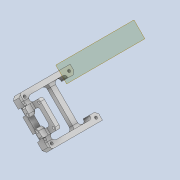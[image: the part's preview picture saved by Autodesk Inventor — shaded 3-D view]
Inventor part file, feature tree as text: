
AUTODESK INVENTOR PART (.ipt)
format: ipt  version: 2020 (Build 240168000, 168)  size: 592,384 bytes
history: native  units: mm
features: projected_geometry x16, sketch x12, extrude x10, thicken_offset x9, fillet x8, other x6, chamfer x5, hole x2, plane x1, reference x1
ambient origin geometry x8: Origin, YZ Plane, XZ Plane, XY Plane, X Axis, Y Axis, Z Axis, Center Point
bodies: Solid1 (feature_tree)
feature tree (70):
  extrude  "Extrusion1"  Depth=4.0mm
  extrude  "Extrusion2"  Depth=4.0mm
  extrude  "Extrusion3"  Depth=2.0mm
  thicken_offset  "Thicken1"
  thicken_offset  "Thicken2"
  thicken_offset  "Thicken3"
  thicken_offset  "Thicken4"
  chamfer  "Chamfer2"  Distance=6.3mm
  fillet  "Fillet5"  Radius=6.0mm
  hole  "Hole1"  [1 undecoded]
  hole  "Hole2"  [1 undecoded]
  plane  "Work Plane1"
  extrude  "Extrusion4"  Depth=0.25mm
  extrude  "Extrusion5"  Depth=0.25mm
  extrude  "Extrusion6"  Depth=1.0mm
  thicken_offset  "Thicken5"
  thicken_offset  "Thicken6"
  thicken_offset  "Thicken7"
  fillet  "Fillet8"  Radius=1.0mm
  chamfer  "Chamfer3"  Distance=1.0mm Angle=45.0deg
  fillet  "Fillet9"  Radius=2.0mm
  fillet  "Fillet10"  Radius=6.0mm
  fillet  "Fillet11"  Radius=6.0mm
  chamfer  "Chamfer4"  Distance=6.0mm
  extrude  "Extrusion7"  Depth=6.0mm
  fillet  "Fillet12"  Radius=35.0mm
  chamfer  "Chamfer5"  Distance=3.5mm
  extrude  "Extrusion8"  Depth=0.5mm
  fillet  "Fillet13"  Radius=3.5mm
  chamfer  "Chamfer6"  Distance=6.3mm
  fillet  "Fillet14"  Radius=6.3mm
  thicken_offset  "Thicken8"
  thicken_offset  "Thicken9"
  extrude  "Extrusion9"  Depth=0.5mm
  extrude  "Extrusion10"  Depth=0.5mm
  sketch  "Sketch1"  dims[d0=4.0mm d1=4.0mm]
  reference  "Reference1"
  sketch  "Sketch2"  dims[d2=4.0mm d3=4.0mm]
  projected_geometry  "Projected Loop1"
  sketch  "Sketch3"  dims[d4=2.0mm d5=0.0mm d6=5.5mm]
  projected_geometry  "Projected Loop2"
  projected_geometry  "Projected Loop3"
  projected_geometry  "Projected Loop4"
  sketch  "Sketch4"  dims[d7=4.0mm]
  projected_geometry  "Projected Loop5"
  projected_geometry  "Projected Loop6"
  sketch  "Sketch5"  dims[d8=4.0mm]
  projected_geometry  "Projected Loop7"
  projected_geometry  "Projected Loop8"
  sketch  "Sketch6"  dims[d9=4.0mm d10=6.3mm d11=0.0mm d12=6.0mm]
  sketch  "Sketch7"  dims[d13=4.0mm d14=6.0mm]
  projected_geometry  "Projected Loop9"
  projected_geometry  "Projected Loop10"
  sketch  "Sketch8"  dims[d15=4.0mm d16=6.0mm d17=0.0mm]
  projected_geometry  "Projected Loop11"
  sketch  "Sketch9"  dims[d21=0.25mm d22=0.25mm]
  projected_geometry  "Projected Loop12"
  sketch  "Sketch10"  dims[d23=0.25mm d24=0.25mm]
  projected_geometry  "Projected Loop13"
  sketch  "Sketch11"  dims[d27=1.0mm d28=1.0mm d29=1.0mm]
  projected_geometry  "Projected Loop14"
  projected_geometry  "Projected Loop15"
  sketch  "Sketch12"  dims[d30=1.0mm d33=1.0mm d34=2.0mm d35=45.0deg d36=2.0mm d37=1.9mm d38=6.0mm d39=4.0mm d40=2.0mm d41=90.0deg d42=4.0mm d43=0.0mm d44=1.9mm d45=6.0mm d46=4.0mm d47=2.0mm d48=90.0deg d49=4.0mm d50=0.0mm d51=6.0mm d52=6.0mm d53=6.0mm d54=6.0mm d55=35.0mm d56=3.5mm d57=35.0mm d58=3.5mm d59=6.3mm d60=0.0mm d61=6.3mm d62=0.0mm d63=1.9mm d64=1.9mm d65=6.3mm d66=0.0mm d69=1.5mm d70=1.5mm d71=1.0mm d72=1.5mm d73=1.0mm d74=1.5mm d75=3.0mm d76=1.0mm d77=2.0mm d78=45.0deg d79=1.0mm d80=0.5mm d81=0.5mm d82=2.0mm d83=2.0mm d84=45.0deg d85=5.0mm d86=5.0mm d87=5.0mm d88=5.0mm d89=2.0mm d90=0.0mm d91=3.0mm d92=1.0mm d93=2.0mm d94=45.0deg d95=7.0mm d96=29.0mm d97=4.0mm d98=3.5mm d99=0.0mm d100=2.2mm d101=2.0mm d102=2.0mm d103=45.0deg d104=2.0mm d105=0.06mm d106=0.06mm d107=0.06mm d108=0.06mm d109=2.0mm d110=2.0mm d111=2.0mm d112=2.0mm d113=8.0mm d114=0.0mm d115=8.0mm d116=10.0mm d117=2.0mm d118=2.0mm d119=8.0mm d120=0.0mm d18=0.5mm d19=0.872665mm]
  projected_geometry  "Projected Loop16"
  parser-record x2  (decoder bookkeeping rows leaked as tree rows — omitted from the tree; the rows remain in map.json)
  other  "mot_27_ass.iam"
  other  "mot_27_2:1"
  other  "tip_3_ass_base.iam"
  other  "ext_shell_2:1"
note: 2 required parameter values undecoded (feature->parameter linkage not recoverable at this tier; creation-order binding heuristic only, values carry confidence <= 0.55)
note: 2 file-system paths scrubbed to <path> (originals preserved in map.json)
